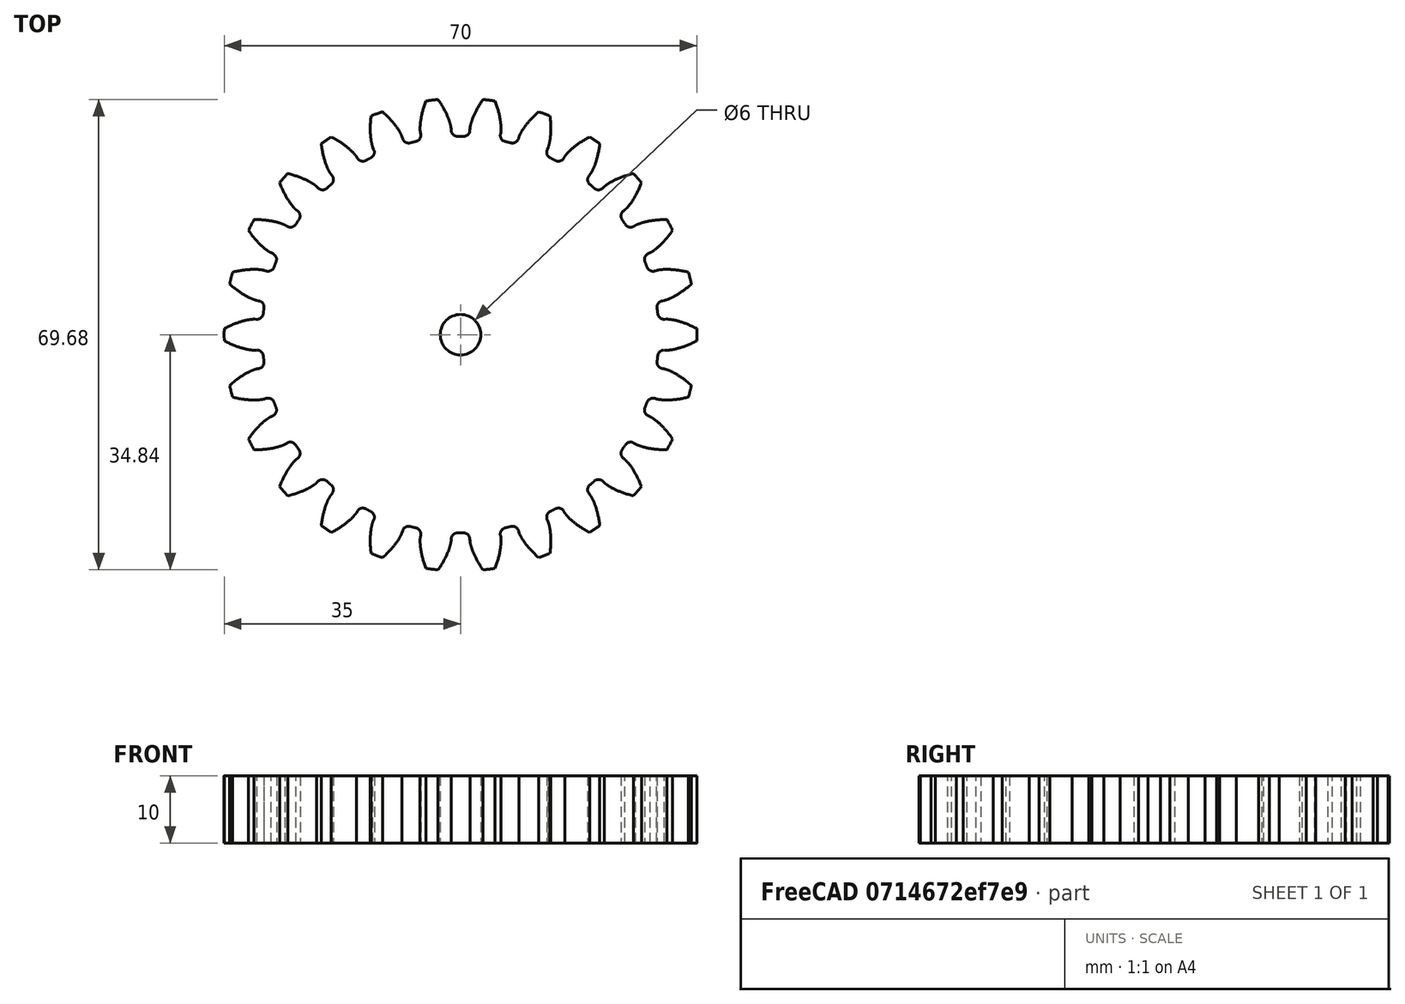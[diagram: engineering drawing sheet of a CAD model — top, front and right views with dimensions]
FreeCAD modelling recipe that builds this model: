
FCSTD DOCUMENT  (FreeCAD 0.19R24276 (Git))
Label: geer
License: All rights reserved
LicenseURL: http://en.wikipedia.org/wiki/All_rights_reserved
objects: Part::Part2DObjectPython×1, PartDesign::Pad×1, Sketcher::SketchObject×1, PartDesign::Hole×1, PartDesign::Body×1, Fem::FemSolverObjectPython×1, Fem::ConstraintFixed×1, Fem::ConstraintPressure×1, App::MaterialObjectPython×1, Fem::FemAnalysis×1
note: 7 computed .brp shape members not serialized (recipe doc carries the construction recipe); baked Part::Feature solids carry a one-line shape summary decoded from their .brp

FEATURE [Part::Part2DObjectPython] InvoluteGear  # Draft 2D object (typed FeaturePython)
  ExternalGear = true
  HighPrecision = true
  Modules = 2.5
  NumberOfTeeth = 26
  PressureAngle = 20
FEATURE [PartDesign::Pad] Pad
  Direction = (1,1,1)
  Length = 10
  Length2 = 100
  Profile = -> InvoluteGear
  Type = 0
FEATURE [Sketcher::SketchObject] Sketch
  FullyConstrained = false
  MapMode = 5
  Placement = pos=(0,0,10) rot=(0,0,1;0rad)
  Support = -> [Pad]
  sketch-geometry (1):
    g0: Circle CenterX=0 CenterY=0 CenterZ=0 NormalX=0 NormalY=0 NormalZ=1 AngleXU=0 Radius=9.97688
  constraints (1):
    c: Coincident(g0,g-1)
FEATURE [PartDesign::Hole] Hole
  BaseFeature = -> Pad
  Depth = 25
  DepthType = 0
  Diameter = 6
  DrillForDepth = false
  DrillPoint = 1
  DrillPointAngle = 118
  HoleCutCountersinkAngle = 90
  HoleCutCustomValues = false
  HoleCutDepth = 0
  HoleCutDiameter = 6.1
  HoleCutType = 0
  ModelActualThread = false
  Profile = -> Sketch
  Tapered = false
  TaperedAngle = 90
  ThreadAngle = 0
  ThreadClass = 0
  ThreadCutOffInner = 0
  ThreadCutOffOuter = 0
  ThreadDirection = 0
  ThreadFit = 0
  ThreadPitch = 0
  ThreadSize = 0
  ThreadType = 0
  Threaded = false
FEATURE [PartDesign::Body] Body
  Group = -> [InvoluteGear,Pad,Sketch,Hole]
  Origin = -> Origin
  Tip = -> Hole
FEATURE [Fem::FemSolverObjectPython] SolverCcxTools  # FEM object (typed FeaturePython)
  AnalysisType = 0
  BeamShellResultOutput3D = false
  EigenmodeHighLimit = 1000000
  EigenmodeLowLimit = 0
  EigenmodesCount = 10
  GeometricalNonlinearity = 0
  IterationsControlParameterCutb = 0.25,0.5,0.75,0.85,,,1.5,
  IterationsControlParameterIter = 4,8,9,200,10,400,,200,,
  IterationsControlParameterTimeUse = false
  IterationsThermoMechMaximum = 2000
  IterationsUserDefinedIncrementations = false
  IterationsUserDefinedTimeStepLength = false
  MaterialNonlinearity = 0
  MatrixSolverType = 1
  SplitInputWriter = false
  ThermoMechSteadyState = true
  TimeEnd = 1
  TimeInitialStep = 0.01
FEATURE [Fem::ConstraintFixed] ConstraintFixed
  NormalDirection = (1,-1e-16,0)
  Normals = (9) [(-1,0,0),(1,-1.22465e-16,0),(-1,2.44929e-16,0),(-1,0,0),(1,-1.22465e-16,0),(-1,2.44929e-16,0),(-1,0,0),(1,-1.22465e-16,0),(-1,2.44929e-16,0)]
  Points = (9) [(3,0,10),(-3,3.67394e-16,10),(3,-7.34788e-16,10),(3,0,5),(-3,3.67394e-16,5),(3,-7.34788e-16,5),(3,0,0),(-3,3.67394e-16,0),(3,-7.34788e-16,0)]
  References = -> [Hole]
FEATURE [Fem::ConstraintPressure] ConstraintPressure
  NormalDirection = (0.967037,0.254634,0)
  Normals = (9) [(0.992714,0.120498,0),(0.967037,0.254634,0),(0.923162,0.384411,0),(0.992714,0.120498,0),(0.967037,0.254634,0),(0.923162,0.384411,0),+3 more]
  Points = (9) [(20.6209,-28.2836,10),(20.239,-26.2495,10),(19.7702,-24.8431,10),(20.6209,-28.2836,5),(20.239,-26.2495,5),(19.7702,-24.8431,5),(20.6209,-28.2836,0),+2 more]
  Pressure = 100
  References = -> [Hole]
FEATURE [App::MaterialObjectPython] MaterialSolid  # material (typed FeaturePython)
  Category = 0
  Material = AuthorAndLicense=Steel-Generic,CardName=Steel-Generic,Density=7900 kg/m^3,+9 more (map truncated)
FEATURE [Fem::FemAnalysis] Analysis
  Group = -> [SolverCcxTools,ConstraintFixed,ConstraintPressure,MaterialSolid]
